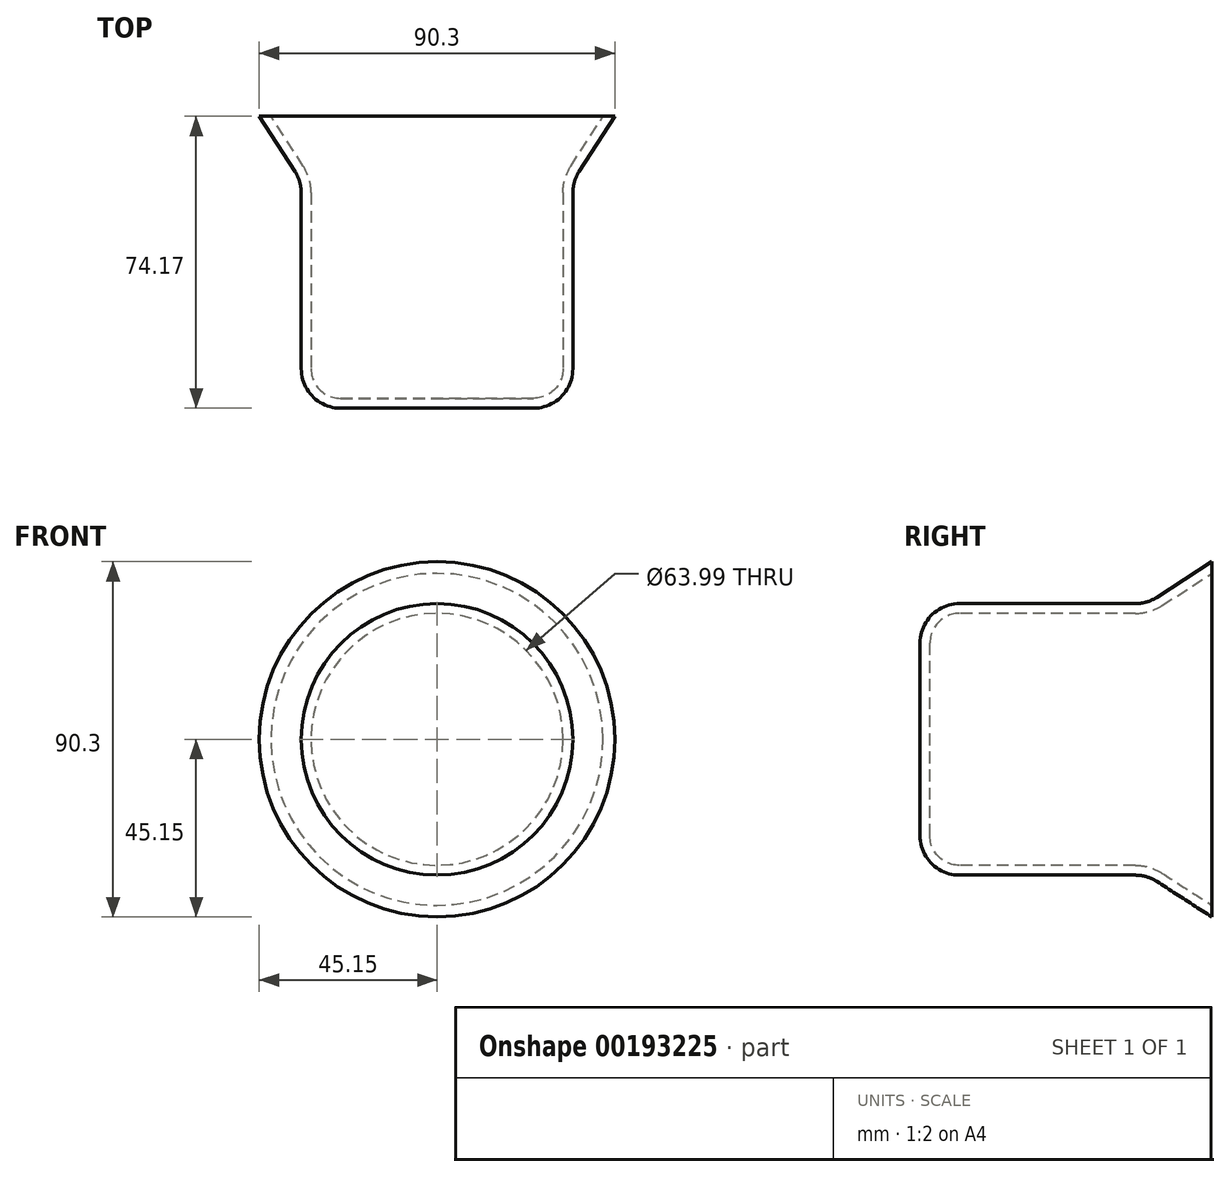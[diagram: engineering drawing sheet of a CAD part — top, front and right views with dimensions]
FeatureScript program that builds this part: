
annotation { "Feature Type Name" : "Feature", "Feature Type Description" : "" }
export const myFeature = defineFeature(function(context is Context, id is Id, definition is map)
    precondition{}
    {
        {
            var Q0;
            Q0=qCreatedBy(makeId("Top.planeOp"),FACE);
            var sketch = newSketch(context, id + "F0", { "sketchPlane" : qUnion([Q0])});
            skLineSegment(sketch, "E0", {"start": v(0, 51.25) * mm, "end": v(45.15, 51.25) * mm});
            skLineSegment(sketch, "E1", {"start": v(45.15, 51.25) * mm, "end": v(36.1, 37.21) * mm});
            skLineSegment(sketch, "E2", {"start": v(34.5, 31.8) * mm, "end": v(34.5, -12.92) * mm});
            skLineSegment(sketch, "E3", {"start": v(24.5, -22.92) * mm, "end": v(0, -22.92) * mm});
            skLineSegment(sketch, "E4", {"start": v(0, -22.92) * mm, "end": v(0, 51.25) * mm});
            skPoint(sketch, "E5.visualSharp", {"position": v(34.5, 34.74) * mm});
            skArc(sketch, "E5.filletArc", {"start": v(36.1, 37.21) * mm, "mid": v(34.9, 34.62) * mm, "end": v(34.5, 31.8) * mm});
            skPoint(sketch, "E6.visualSharp", {"position": v(34.5, -22.92) * mm});
            skArc(sketch, "E6.filletArc", {"start": v(24.5, -22.92) * mm, "mid": v(31.57, -19.99) * mm, "end": v(34.5, -12.92) * mm});
            skSolve(sketch);
        }
        {
            var Q0;
            Q0=makeQuery(id+"F0.imprint","IMPRINT",FACE,{"disambiguationData":[TD([[makeQuery(id+"F0.imprint","IMPRINT",EDGE,{"derivedFrom":sQuery(id+"F0.wireOp",EDGE,"E0")}),-1.0]])]});
            var Q1;
            Q1=sQuery(id+"F0.wireOp",EDGE,"E4");
            revolve(context, id + "F1", {"entities" : qUnion([Q0]), "axis" : qUnion([Q1]), "revolveType" : RevolveType.FULL});
        }
        {
            var Q0;
            Q0=makeQuery(id+"F1.opRevolve","SWEPT_FACE",FACE,{"disambiguationData":[OSD([sQuery(id+"F0.wireOp",EDGE,"E0")])]});
            shell(context, id + "F2", {"entities" : qUnion([Q0]), "thickness" : 2.5 * mm});
        }
    });
